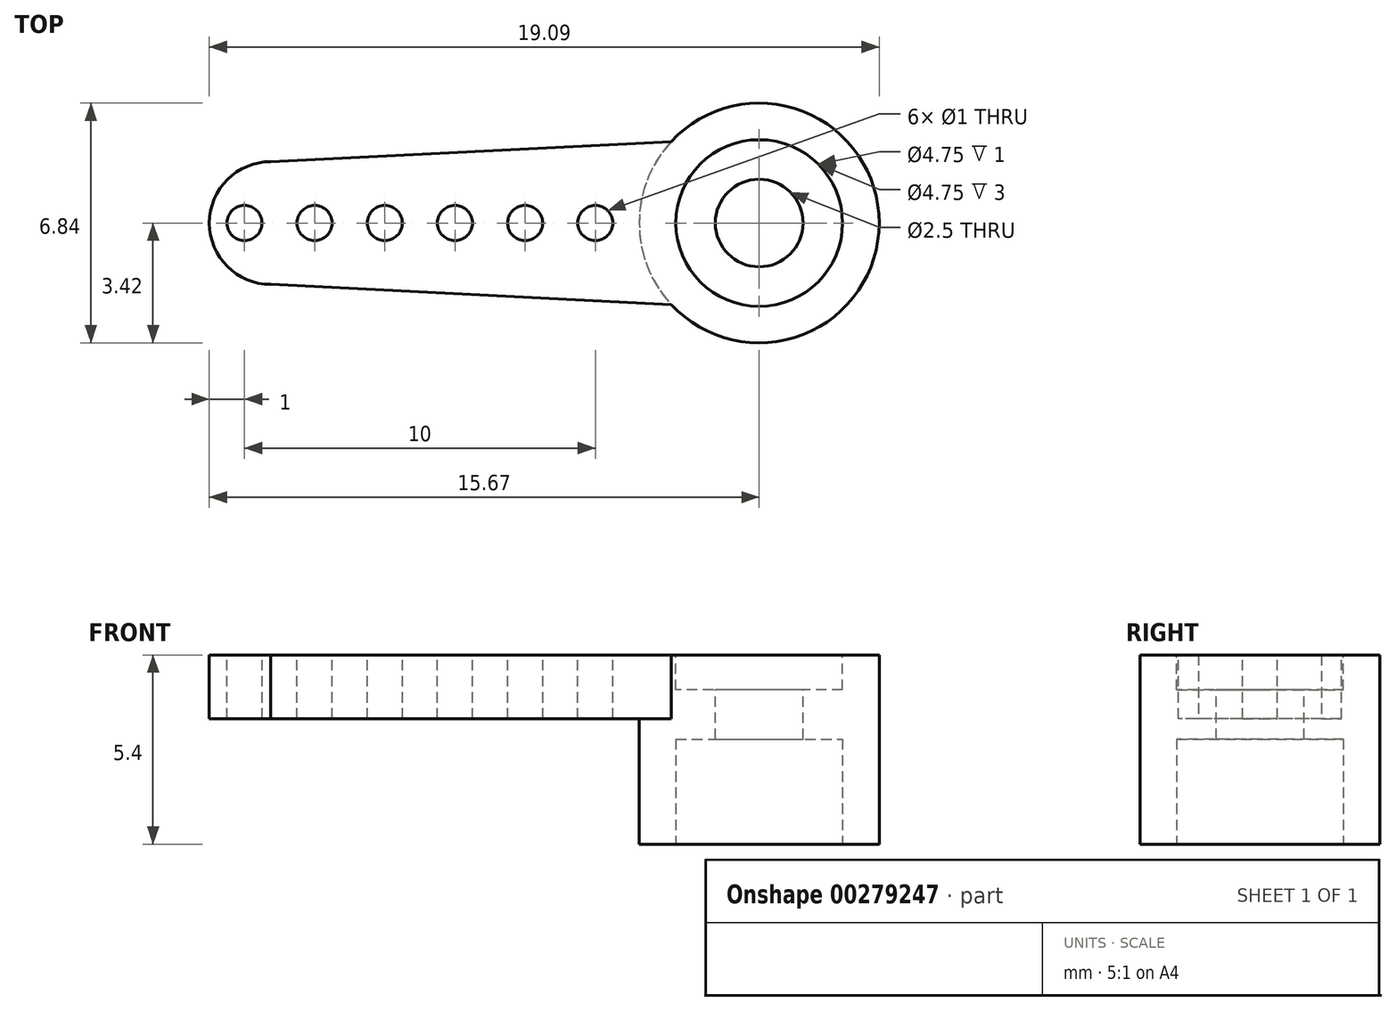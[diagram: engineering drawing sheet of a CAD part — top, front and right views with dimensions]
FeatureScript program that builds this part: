
annotation { "Feature Type Name" : "Feature", "Feature Type Description" : "" }
export const myFeature = defineFeature(function(context is Context, id is Id, definition is map)
    precondition{}
    {
        {
            var Q0;
            Q0=qCreatedBy(makeId("Top.planeOp"),FACE);
            var sketch = newSketch(context, id + "F0", { "sketchPlane" : qUnion([Q0])});
            skCircle(sketch, "E0", {"center": v(-13.92, 0) * mm, "radius": 1.75 * mm});
            skLineSegment(sketch, "E1", {"start": v(0, 2.45) * mm, "end": v(0, -2.45) * mm});
            skLineSegment(sketch, "E2", {"start": v(-13.92, -1.75) * mm, "end": v(-13.92, 1.75) * mm});
            skLineSegment(sketch, "E3", {"start": v(-13.92, 1.75) * mm, "end": v(0, 2.45) * mm});
            skLineSegment(sketch, "E4", {"start": v(-13.92, -1.75) * mm, "end": v(0, -2.45) * mm});
            skSolve(sketch);
        }
        {
            var Q0;
            {var subQ0=sQuery(id+"F0.wireOp",EDGE,"E2");Q0=makeQuery(id+"F0.imprint","IMPRINT",FACE,{"disambiguationData":[TD([[makeQuery(id+"F0.imprint","IMPRINT",EDGE,{"derivedFrom":subQ0}),1.0]])]});}
            var Q1;
            Q1=makeQuery(id+"F0.imprint","IMPRINT",FACE,{"disambiguationData":[TD([[makeQuery(id+"F0.imprint","IMPRINT",EDGE,{"derivedFrom":sQuery(id+"F0.wireOp",EDGE,"E1")}),-1.0]])]});
            var Q2;
            {var subQ0=sQuery(id+"F0.wireOp",EDGE,"E2");Q2=makeQuery(id+"F0.imprint","IMPRINT",FACE,{"disambiguationData":[TD([[makeQuery(id+"F0.imprint","IMPRINT",EDGE,{"derivedFrom":subQ0}),-1.0]])]});}
            extrude(context, id + "F1", {"entities" : qUnion([Q0, Q1, Q2]), "endBound" : BoundingType.SYMMETRIC, "depth" : 1.82 * mm});
        }
        {
            var Q0;
            Q0=makeQuery(id+"F1.opExtrude","CAP_FACE",FACE,{"disambiguationData":[OSD([sQuery(id+"F0.wireOp",EDGE,"E0"),sQuery(id+"F0.wireOp",EDGE,"E1"),sQuery(id+"F0.wireOp",EDGE,"E3"),sQuery(id+"F0.wireOp",EDGE,"E4")])],"isStart":false});
            var sketch = newSketch(context, id + "F2", { "sketchPlane" : qUnion([Q0])});
            skCircle(sketch, "E5", {"center": v(0, 0) * mm, "radius": 3.42 * mm});
            skSolve(sketch);
        }
        {
            var Q0;
            {var subQ5=makeQuery(id+"F1.opExtrude","CAP_EDGE",EDGE,{"disambiguationData":[OSD([sQuery(id+"F0.wireOp",EDGE,"E1")])],"isStart":false});Q0=makeQuery(id+"F2.imprint","IMPRINT",FACE,{"disambiguationData":[TD([[makeQuery(id+"F2.imprint","IMPRINT",EDGE,{"derivedFrom":subQ5}),-1.0]])]});}
            var Q1;
            {var subQ5=makeQuery(id+"F1.opExtrude","CAP_EDGE",EDGE,{"disambiguationData":[OSD([sQuery(id+"F0.wireOp",EDGE,"E1")])],"isStart":false});Q1=makeQuery(id+"F2.imprint","IMPRINT",FACE,{"disambiguationData":[TD([[makeQuery(id+"F2.imprint","IMPRINT",EDGE,{"derivedFrom":subQ5}),1.0]])]});}
            extrude(context, id + "F3", {"entities" : qUnion([Q0, Q1]), "operationType" : NewBodyOperationType.ADD, "oppositeDirection" : true, "depth" : 5.4 * mm});
        }
        {
            var Q0;
            Q0=makeQuery(id+"F3.boolean.opBoolean","MERGE",FACE,{"derivedFrom":[makeQuery(id+"F1.opExtrude","CAP_FACE",FACE,{"disambiguationData":[OSD([sQuery(id+"F0.wireOp",EDGE,"E0"),sQuery(id+"F0.wireOp",EDGE,"E1"),sQuery(id+"F0.wireOp",EDGE,"E3"),sQuery(id+"F0.wireOp",EDGE,"E4")])],"isStart":false}),makeQuery(id+"F3.opExtrude","CAP_FACE",FACE,{"disambiguationData":[OSD([sQuery(id+"F2.wireOp",EDGE,"E5")])],"isStart":true})]});
            var sketch = newSketch(context, id + "F4", { "sketchPlane" : qUnion([Q0])});
            skCircle(sketch, "E6", {"center": v(0, 0) * mm, "radius": 2.38 * mm});
            skSolve(sketch);
        }
        {
            var Q0;
            Q0=makeQuery(id+"F4.imprint","IMPRINT",FACE,{"disambiguationData":[TD([[makeQuery(id+"F4.imprint","IMPRINT",EDGE,{"derivedFrom":sQuery(id+"F4.wireOp",EDGE,"E6")}),1.0]])]});
            extrude(context, id + "F5", {"entities" : qUnion([Q0]), "operationType" : NewBodyOperationType.REMOVE, "oppositeDirection" : true, "depth" : 1 * mm});
        }
        {
            var Q0;
            Q0=makeQuery(id+"F3.opExtrude","CAP_FACE",FACE,{"disambiguationData":[OSD([sQuery(id+"F2.wireOp",EDGE,"E5")])],"isStart":false});
            var sketch = newSketch(context, id + "F6", { "sketchPlane" : qUnion([Q0])});
            skCircle(sketch, "E7", {"center": v(0, 0) * mm, "radius": 2.38 * mm});
            skSolve(sketch);
        }
        {
            var Q0;
            Q0=makeQuery(id+"F6.imprint","IMPRINT",FACE,{"disambiguationData":[TD([[makeQuery(id+"F6.imprint","IMPRINT",EDGE,{"derivedFrom":sQuery(id+"F6.wireOp",EDGE,"E7")}),1.0]])]});
            extrude(context, id + "F7", {"entities" : qUnion([Q0]), "operationType" : NewBodyOperationType.REMOVE, "oppositeDirection" : true, "depth" : 3 * mm});
        }
        {
            var Q0;
            Q0=makeQuery(id+"F5.boolean.opBoolean","COPY",FACE,{"derivedFrom":makeQuery(id+"F5.opExtrude","CAP_FACE",FACE,{"disambiguationData":[OSD([sQuery(id+"F4.wireOp",EDGE,"E6")])],"isStart":false})});
            var sketch = newSketch(context, id + "F8", { "sketchPlane" : qUnion([Q0])});
            skCircle(sketch, "E8", {"center": v(0, 0) * mm, "radius": 1.25 * mm});
            skSolve(sketch);
        }
        {
            var Q0;
            Q0=sQuery(id+"F8.wireOp",VERTEX,"E8.center");
            var Q1;
            Q1=makeQuery(id+"F1.opExtrude","SWEPT_BODY",BODY,{"disambiguationData":[OSD([sQuery(id+"F0.wireOp",EDGE,"E0"),sQuery(id+"F0.wireOp",EDGE,"E1"),sQuery(id+"F0.wireOp",EDGE,"E3"),sQuery(id+"F0.wireOp",EDGE,"E4")])]});
            hole(context, id + "F9", {"style" : HoleStyle.SIMPLE, "endStyle" : HoleEndStyle.THROUGH, "holeDiameter" : 2.5 * mm, "tappedDepth" : 12 * mm, "tapClearance" : 3, "locations" : qUnion([Q0]), "scope" : qUnion([Q1])});
        }
        {
            var Q0;
            Q0=makeQuery(id+"F3.boolean.opBoolean","MERGE",FACE,{"derivedFrom":[makeQuery(id+"F1.opExtrude","CAP_FACE",FACE,{"disambiguationData":[OSD([sQuery(id+"F0.wireOp",EDGE,"E0"),sQuery(id+"F0.wireOp",EDGE,"E1"),sQuery(id+"F0.wireOp",EDGE,"E3"),sQuery(id+"F0.wireOp",EDGE,"E4")])],"isStart":false}),makeQuery(id+"F3.opExtrude","CAP_FACE",FACE,{"disambiguationData":[OSD([sQuery(id+"F2.wireOp",EDGE,"E5")])],"isStart":true})]});
            var sketch = newSketch(context, id + "F10", { "sketchPlane" : qUnion([Q0])});
            skCircle(sketch, "E9", {"center": v(-14.67, 0) * mm, "radius": 0.5 * mm});
            skCircle(sketch, "E10", {"center": v(-12.67, 0) * mm, "radius": 0.5 * mm});
            skCircle(sketch, "E11", {"center": v(-10.67, 0) * mm, "radius": 0.5 * mm});
            skCircle(sketch, "E12", {"center": v(-8.67, 0) * mm, "radius": 0.5 * mm});
            skCircle(sketch, "E13", {"center": v(-6.67, 0) * mm, "radius": 0.5 * mm});
            skCircle(sketch, "E14", {"center": v(-4.67, 0) * mm, "radius": 0.5 * mm});
            skSolve(sketch);
        }
        {
            var Q0;
            Q0=sQuery(id+"F10.wireOp",VERTEX,"E9.center");
            var Q1;
            Q1=sQuery(id+"F10.wireOp",VERTEX,"E10.center");
            var Q2;
            Q2=sQuery(id+"F10.wireOp",VERTEX,"E11.center");
            var Q3;
            Q3=sQuery(id+"F10.wireOp",VERTEX,"E12.center");
            var Q4;
            Q4=sQuery(id+"F10.wireOp",VERTEX,"E13.center");
            var Q5;
            Q5=sQuery(id+"F10.wireOp",VERTEX,"E14.center");
            var Q6;
            Q6=makeQuery(id+"F1.opExtrude","SWEPT_BODY",BODY,{"disambiguationData":[OSD([sQuery(id+"F0.wireOp",EDGE,"E0"),sQuery(id+"F0.wireOp",EDGE,"E1"),sQuery(id+"F0.wireOp",EDGE,"E3"),sQuery(id+"F0.wireOp",EDGE,"E4")])]});
            hole(context, id + "F11", {"style" : HoleStyle.SIMPLE, "endStyle" : HoleEndStyle.THROUGH, "holeDiameter" : 1 * mm, "tappedDepth" : 12 * mm, "tapClearance" : 3, "locations" : qUnion([Q0, Q1, Q2, Q3, Q4, Q5]), "scope" : qUnion([Q6])});
        }
    });
